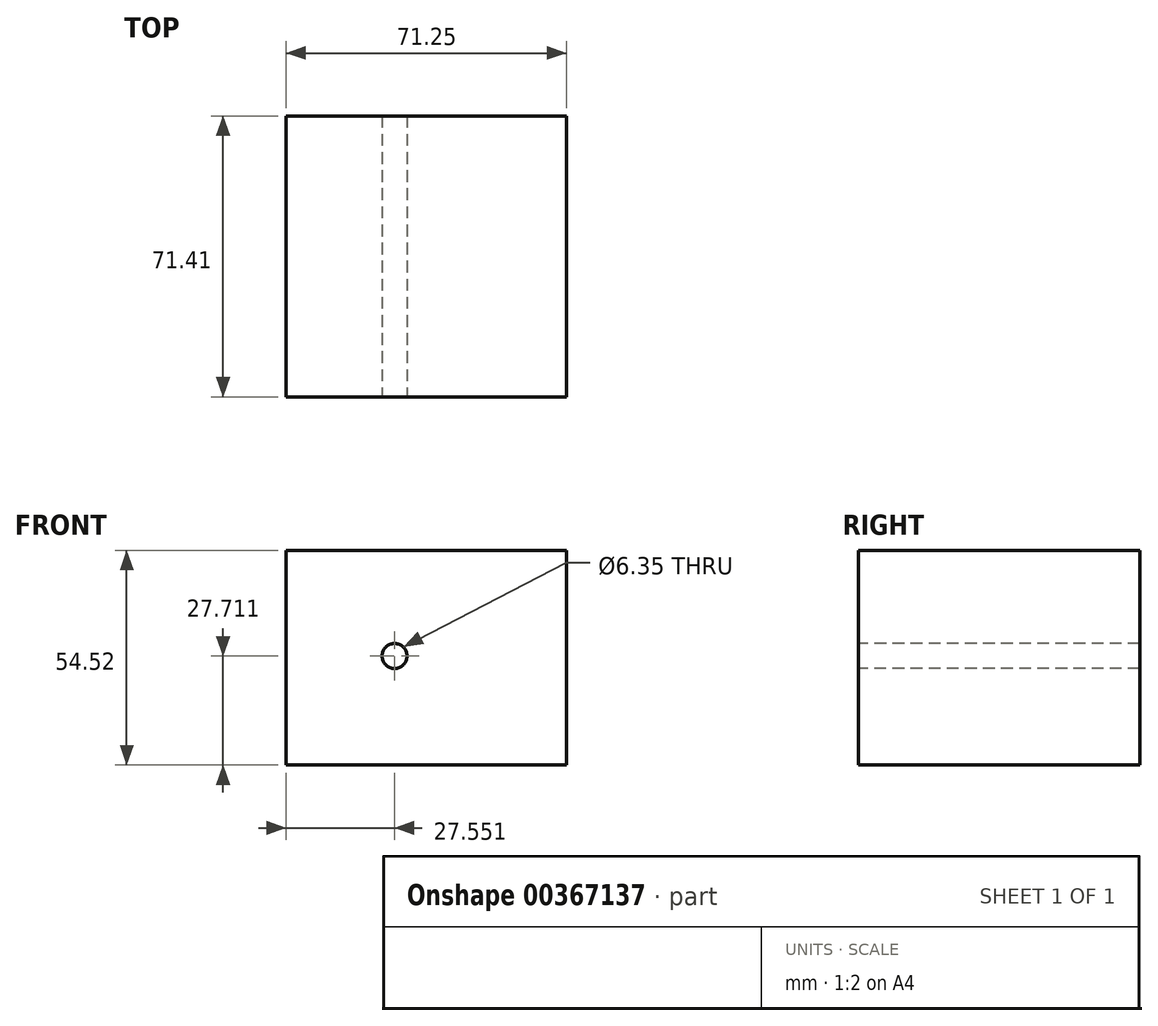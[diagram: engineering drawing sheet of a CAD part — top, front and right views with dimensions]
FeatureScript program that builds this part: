
annotation { "Feature Type Name" : "Feature", "Feature Type Description" : "" }
export const myFeature = defineFeature(function(context is Context, id is Id, definition is map)
    precondition{}
    {
        {
            var Q0;
            Q0=qCreatedBy(makeId("Front.planeOp"),FACE);
            var sketch = newSketch(context, id + "F0", { "sketchPlane" : qUnion([Q0])});
            skLineSegment(sketch, "E0.bottom", {"start": v(-55.97, 54.52) * mm, "end": v(15.28, 54.52) * mm});
            skLineSegment(sketch, "E0.top", {"start": v(-55.97, 0) * mm, "end": v(15.28, 0) * mm});
            skLineSegment(sketch, "E0.left", {"start": v(-55.97, 54.52) * mm, "end": v(-55.97, 0) * mm});
            skLineSegment(sketch, "E0.right", {"start": v(15.28, 54.52) * mm, "end": v(15.28, 0) * mm});
            skSolve(sketch);
        }
        {
            var Q0;
            Q0 = qSketchRegion(id + "F0", true);
            extrude(context, id + "F1", {"entities" : qUnion([Q0]), "depth" : 71.4 * mm});
        }
        {
            var Q0;
            Q0=makeQuery(id+"F1.opExtrude","CAP_FACE",FACE,{"disambiguationData":[OSD([sQuery(id+"F0.wireOp",EDGE,"E0.bottom"),sQuery(id+"F0.wireOp",EDGE,"E0.top"),sQuery(id+"F0.wireOp",EDGE,"E0.left"),sQuery(id+"F0.wireOp",EDGE,"E0.right")])],"isStart":false});
            var sketch = newSketch(context, id + "F2", { "sketchPlane" : qUnion([Q0])});
            skCircle(sketch, "E1", {"center": v(-28.42, 27.71) * mm, "radius": 24.57 * mm});
            skSolve(sketch);
        }
        {
            var Q0;
            Q0=sQuery(id+"F2.wireOp",VERTEX,"E1.center");
            var Q1;
            Q1=makeQuery(id+"F1.opExtrude","SWEPT_BODY",BODY,{"disambiguationData":[OSD([sQuery(id+"F0.wireOp",EDGE,"E0.bottom"),sQuery(id+"F0.wireOp",EDGE,"E0.top"),sQuery(id+"F0.wireOp",EDGE,"E0.left"),sQuery(id+"F0.wireOp",EDGE,"E0.right")])]});
            hole(context, id + "F3", {"style" : HoleStyle.SIMPLE, "endStyle" : HoleEndStyle.THROUGH, "holeDiameter" : 6.35 * mm, "isTappedThrough" : true, "tappedDepth" : 12.7 * mm, "tapClearance" : 3, "locations" : qUnion([Q0]), "scope" : qUnion([Q1])});
        }
    });
